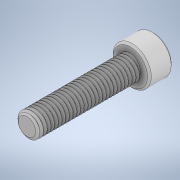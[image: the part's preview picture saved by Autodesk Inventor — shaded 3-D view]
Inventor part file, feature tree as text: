
AUTODESK INVENTOR PART (.ipt)
format: ipt  version: 2021 (Build 250183000, 183)  size: 893,952 bytes
history: native  units: in
note: dims shown in document units (in); Inventor stores cm internally (conversion verified against a paired STEP export)
features: chamfer x1
ambient origin geometry x8: Origin, YZ Plane, XZ Plane, XY Plane, X Axis, Y Axis, Z Axis, Center Point
bodies: Solid1 (feature_tree)
feature tree (1):
  chamfer  "Chamfer1"  [1 undecoded]
note: 1 required parameter value undecoded (feature->parameter linkage not recoverable at this tier; creation-order binding heuristic only, values carry confidence <= 0.55)
